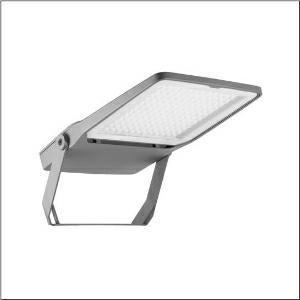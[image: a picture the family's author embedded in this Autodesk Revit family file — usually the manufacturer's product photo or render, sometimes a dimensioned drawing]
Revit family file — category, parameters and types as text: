
# Revit family: floodlight_fl_20_midi___rs17_5xa7682e1b1ac_fe9e
name_source: partatom
category: Lighting Fixtures
units: mm (PartAtom-declared; Revit-internal decimal feet)

## family parameters
Cut with Voids When Loaded = No
Host = Face
Light Source = No
Part Type = Normal
Room Calculation Point = No
Round Connector Dimension = Use Diameter
Shared = No

## types (1)
- --- (1 x LED 3000K / CRI = 80 (unbekannt), 22840 lm, 3000K)
    Apparent Load = 208 VA
    CIE Flux Codes = 79 92 99 100 100
    Color Rendering = 80
    Color Temperature = 3000K
    Default Elevation = 1800 mm
    Description = Floodlight FL 20 midi, floodlight, primary light control with lens, of plastic, primary optical cover: protective disc, of toughened safety glass, transparent, light distribution: RS17, light emission: direct distribution, primary light characteristic: rotationally symmetric, installation type: surface-mounted, LED High Power LED, rated luminous flux: 22.840 lm, light colour: 830, colour temperature: 3000K, control gear: ECG Plus, control: flexible luminous flux parameterisation, time-dependent luminous flux control, digital communication interface, power reduction, overheat protection, electronic power reduction, with terminal, 5-pole, max. 2.5mm², mains connection: 220..240V, AC, 50/60Hz, rated input power: 208W, LED unit, of diecast aluminium, powder-coated, Siteco® metallic grey (DB 702S), length: 654 mm, width: 450 mm, height: 76mm, housing frame, of diecast aluminium, powder-coated, Siteco® metallic grey (DB 702S), mounting bracket, of steel, powder-coated, Siteco® metallic grey (DB 702S), DALIprotection rating (complete): IP66, insulation class (complete): insulation class II (safety insulation), certification: CE, ENEC, VDE, protection symbol: D, permissible ambient temperature for indoor applications: -40..+40°C, permissible ambient temperature for outdoor applications: -40..+50°C, standard: DIN EN 12944, packaging unit: 1 piece

Light Distribution: RS17
    Height = 76 mm
    Lamp = 1 x LED 3000K / CRI >= 80 (unbekannt)
    Lamp Light Flux = 22840 lm
    Lamp count = 1
    Length = 672 mm
    Luminous efficacy = 110 lm/W
    Manufacturer = Siteco
    ModVariant = No
    Model = 5XA7682E1B1AC
    Number of Poles = 1
    OnlyDefault = Yes
    Power Factor = 1
    Product Name = Floodlight FL 20 midi | RS17
    Product group = floodlight | pylon top
    ProductGroupID = 6101
    Protection Class = Protection class II
    Protection Degree = IP 66
    RLX_Detail_Level = 1
    RlxData = <blob elided: 92081 chars, md5=0153ea3f>
    Socket = socket
    Standby Power = 0 W
    System Light Flux = 22840 lm
    System Power = 208 W
    Type Comments = factory setting: luminous flux: 100 % | dim-lin: 254 | 484 mA
    Type Image = l_1005943.jpg
    URL = http://relux.com
    VarID = @adj_141885
    Voltage = 0 V
    Weight = 0.00 kg
    Width = 450 mm

## geometry (parser evidence)
native form markers: Blend x4, Sweep x13
no freeform markers — native parametric forms only
